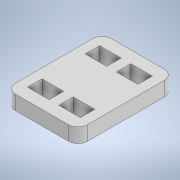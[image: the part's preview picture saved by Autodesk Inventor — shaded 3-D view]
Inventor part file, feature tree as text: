
AUTODESK INVENTOR PART (.ipt)
format: ipt  version: 2020 (Build 240168000, 168)  size: 125,952 bytes
history: native  units: in
note: dims shown in document units (in); Inventor stores cm internally (conversion verified against a paired STEP export)
features: extrude x1, sketch x1
ambient origin geometry x8: Origin, YZ Plane, XZ Plane, XY Plane, X Axis, Y Axis, Z Axis, Center Point
bodies: Solid1 (feature_tree)
feature tree (2):
  extrude  "Extrusion1"  Depth=0.0787in
  sketch  "Sketch1"  dims[d2=0.0787in d3=0.0787in d4=0.6299in d5=0.4331in d9=0.1772in d10=0.1181in d11=0.0984in d12=0.0787in d13=0.1181in d14=0.0in d6=0.0197in d7=0.0344in d8=0.0197in]
